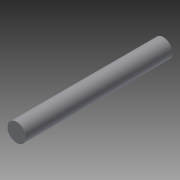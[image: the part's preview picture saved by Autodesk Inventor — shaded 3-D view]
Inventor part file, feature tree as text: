
AUTODESK INVENTOR PART (.ipt)
format: ipt  version: 2014 (Build 180170000, 170)  size: 69,120 bytes
history: native  units: in
note: dims shown in document units (in); Inventor stores cm internally (conversion verified against a paired STEP export)
features: extrude x1, sketch x1
ambient origin geometry x8: Origin, YZ Plane, XZ Plane, XY Plane, X Axis, Y Axis, Z Axis, Center Point
bodies: Solid1 (feature_tree)
feature tree (2):
  extrude  "Extrusion1"  Depth=2.0in TaperAngle=0.0deg
  sketch  "Sketch1"  dims[d0=0.25in d1=2.0in d2=0.0in]
